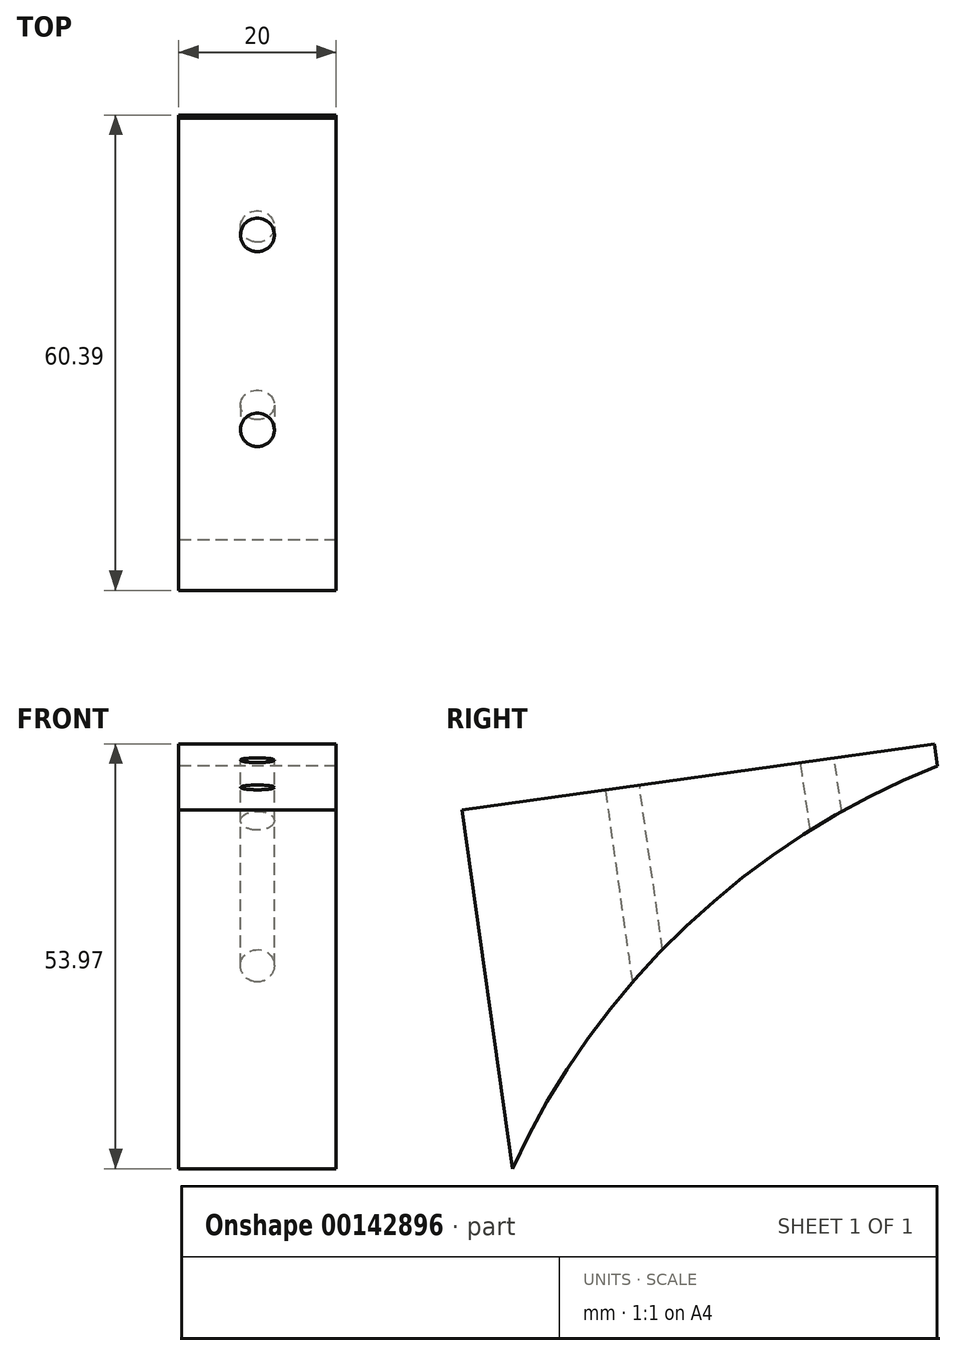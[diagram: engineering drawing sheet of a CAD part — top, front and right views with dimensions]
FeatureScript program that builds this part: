
annotation { "Feature Type Name" : "Feature", "Feature Type Description" : "" }
export const myFeature = defineFeature(function(context is Context, id is Id, definition is map)
    precondition{}
    {
        {
            var Q0;
            Q0=qCreatedBy(makeId("Right.planeOp"),FACE);
            var sketch = newSketch(context, id + "F0", { "sketchPlane" : qUnion([Q0])});
            skCircle(sketch, "E0", {"center": v(0, 0) * mm, "radius": 100 * mm});
            skLineSegment(sketch, "E1", {"start": v(0, -100) * mm, "end": v(-400, -100) * mm});
            skLineSegment(sketch, "E2", {"start": v(-400, -100) * mm, "end": v(-400, 45) * mm});
            skLineSegment(sketch, "E3", {"start": v(-400, 45) * mm, "end": v(32.02, 105.46) * mm});
            skLineSegment(sketch, "E4.0", {"start": v(-402.77, 64.8) * mm, "end": v(29.25, 125.26) * mm});
            skLineSegment(sketch, "E5", {"start": v(-43.02, 115.15) * mm, "end": v(35, -93.67) * mm});
            skLineSegment(sketch, "E6", {"start": v(-100, 107.18) * mm, "end": v(-90.85, 41.79) * mm});
            skLineSegment(sketch, "E7", {"start": v(-40, 115.57) * mm, "end": v(-36.84, 92.97) * mm});
            skSolve(sketch);
        }
        {
            var Q0;
            Q0=qCreatedBy(makeId("Right.planeOp"),FACE);
            var sketch = newSketch(context, id + "F1", { "sketchPlane" : qUnion([Q0])});
            skLineSegment(sketch, "E8.0", {"start": v(-97.23, 87.37) * mm, "end": v(-37.23, 95.76) * mm});
            skArc(sketch, "E9.0", {"start": v(-36.84, 92.97) * mm, "mid": v(-68.78, 72.59) * mm, "end": v(-90.85, 41.79) * mm});
            skLineSegment(sketch, "E10.0", {"start": v(-97.23, 87.37) * mm, "end": v(-90.85, 41.79) * mm});
            skLineSegment(sketch, "E11.0", {"start": v(-37.23, 95.76) * mm, "end": v(-36.84, 92.97) * mm});
            skPoint(sketch, "E12.orphan", {"position": v(-402.77, 64.8) * mm});
            skPoint(sketch, "E13.orphan", {"position": v(-400, 45) * mm});
            skSolve(sketch);
        }
        {
            var Q0;
            Q0 = qSketchRegion(id + "F1", true);
            extrude(context, id + "F2", {"entities" : qUnion([Q0]), "depth" : 20 * mm});
        }
        {
            var Q0;
            Q0=makeQuery(id+"F2.opExtrude","SWEPT_FACE",FACE,{"disambiguationData":[OSD([sQuery(id+"F1.wireOp",EDGE,"E8.0")])]});
            var sketch = newSketch(context, id + "F3", { "sketchPlane" : qUnion([Q0])});
            skCircle(sketch, "E14", {"center": v(10, -38.6) * mm, "radius": 2.15 * mm});
            skLineSegment(sketch, "E15", {"start": v(10, -23.6) * mm, "end": v(10, -38.6) * mm, "construction": true});
            skLineSegment(sketch, "E16", {"start": v(10, -38.6) * mm, "end": v(10, -63.6) * mm, "construction": true});
            skCircle(sketch, "E17", {"center": v(10, -63.6) * mm, "radius": 2.15 * mm});
            skSolve(sketch);
        }
        {
            var Q0;
            Q0 = qSketchRegion(id + "F3", true);
            extrude(context, id + "F4", {"entities" : qUnion([Q0]), "operationType" : NewBodyOperationType.REMOVE, "endBound" : BoundingType.THROUGH_ALL, "oppositeDirection" : true, "depth" : 25 * mm});
        }
    });
